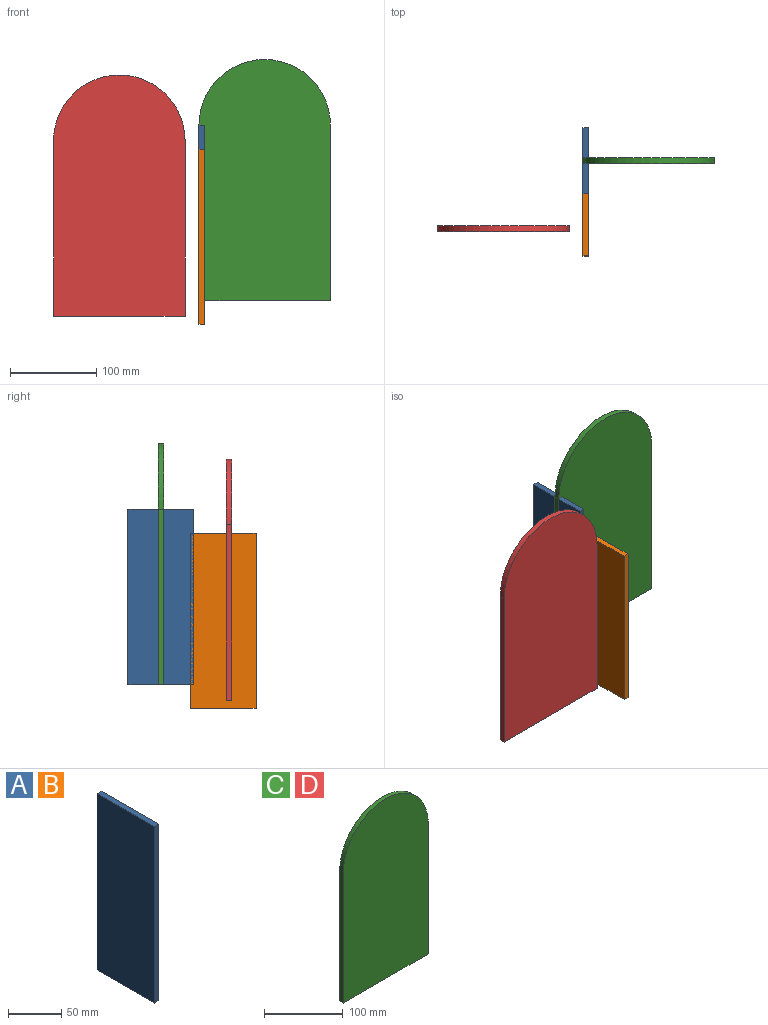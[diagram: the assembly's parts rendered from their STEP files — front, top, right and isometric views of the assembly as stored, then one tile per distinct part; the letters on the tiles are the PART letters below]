
ASSEMBLY  parts=4 mates=1
PART A: 6 faces, bbox 6.4x76.2x203.2 mm
  f0: plane 76.2x6.35mm, normal (0,0,1), area 483.9mm2, adj f1,f3,f4,f5
  f1: plane 203.2x6.35mm, normal (0,-1,0), area 1290.3mm2, adj f0,f2,f4,f5
  f2: plane 76.2x6.35mm, normal (0,0,-1), area 483.9mm2, adj f1,f3,f4,f5
  f3: plane 203.2x6.35mm, normal (0,1,0), area 1290.3mm2, adj f0,f2,f4,f5
  f4: plane 203.2x76.2mm, normal (1,0,0), area 15483.8mm2, adj f0,f1,f2,f3
  f5: plane 203.2x76.2mm, normal (-1,0,0), area 15483.8mm2, adj f0,f1,f2,f3
PART B: same geometry as A
PART C: 6 faces, bbox 152.4x6.4x279.4 mm
  f0: plane 203.2x6.35mm, normal (1,0,0), area 1290.3mm2, adj f1,f3,f4,f5
  f1: cylinder r=76.2mm len=152.4mm, axis (0,1,0), area 1520.1mm2, adj f0,f2,f4,f5
  f2: plane 203.2x6.35mm, normal (-1,0,0), area 1290.3mm2, adj f1,f3,f4,f5
  f3: plane 152.4x6.35mm, normal (0,0,-1), area 967.7mm2, adj f0,f2,f4,f5
  f4: plane 279.4x152.4mm, normal (0,-1,0), area 40088.4mm2, adj f0,f1,f2,f3
  f5: plane 279.4x152.4mm, normal (0,1,0), area 40088.4mm2, adj f0,f1,f2,f3
PART D: same geometry as C
PLACE A t=(0,72.2,27.69)mm
PLACE B at identity
PLACE C t=(168.44,78.75,17.98)mm
PLACE D at identity
MATE fastened C.f2 <-> A.f5  axis (-1,0,0) through (0,75.57,97.2)mm
